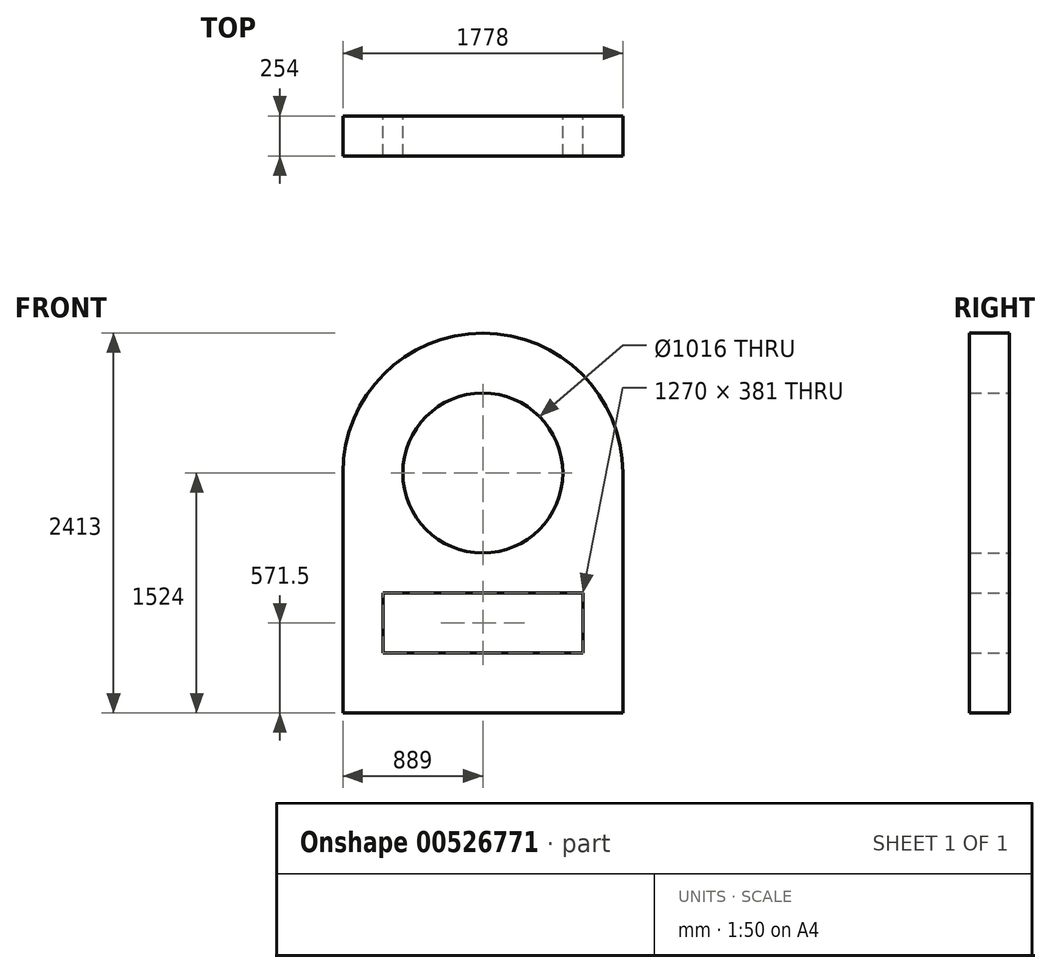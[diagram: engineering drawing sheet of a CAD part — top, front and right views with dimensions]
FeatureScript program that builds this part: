
annotation { "Feature Type Name" : "Feature", "Feature Type Description" : "" }
export const myFeature = defineFeature(function(context is Context, id is Id, definition is map)
    precondition{}
    {
        {
            var Q0;
            Q0=qCreatedBy(makeId("Front.planeOp"),FACE);
            var sketch = newSketch(context, id + "F0", { "sketchPlane" : qUnion([Q0])});
            skLineSegment(sketch, "E0", {"start": v(0, 0) * mm, "end": v(1778, 0) * mm});
            skLineSegment(sketch, "E1", {"start": v(0, 0) * mm, "end": v(0, 1524) * mm});
            skLineSegment(sketch, "E2", {"start": v(1778, 0) * mm, "end": v(1778, 1524) * mm});
            skArc(sketch, "E3", {"start": v(1778, 1524) * mm, "mid": v(889, 2413) * mm, "end": v(0, 1524) * mm});
            skCircle(sketch, "E4", {"center": v(889, 1524) * mm, "radius": 508 * mm});
            skLineSegment(sketch, "E5", {"start": v(254, 762) * mm, "end": v(254, 381) * mm});
            skLineSegment(sketch, "E6", {"start": v(254, 381) * mm, "end": v(1524, 381) * mm});
            skLineSegment(sketch, "E7", {"start": v(1524, 381) * mm, "end": v(1524, 762) * mm});
            skLineSegment(sketch, "E8", {"start": v(1524, 762) * mm, "end": v(254, 762) * mm});
            skSolve(sketch);
        }
        {
            var Q0;
            Q0=makeQuery(id+"F0.imprint","IMPRINT",FACE,{"disambiguationData":[TD([[makeQuery(id+"F0.imprint","IMPRINT",EDGE,{"derivedFrom":sQuery(id+"F0.wireOp",EDGE,"E0")}),1.0]])]});
            extrude(context, id + "F1", {"entities" : qUnion([Q0]), "depth" : 254 * mm, "offsetDistance" : 25.4 * mm});
        }
    });
